# Revit family: Electronics_Commercial-Loudspeakers_Biamp_Small-Design-Loudspeaker_OVO5T
name_source: partatom
category: Communication Devices
units: mm (PartAtom-declared; Revit-internal decimal feet)

## family parameters
Cut with Voids When Loaded = No
Host = Face
Maintain Annotation Orientation = No
OmniClass Number = 23.85.10.11.14.14.14
Part Type = Normal
Room Calculation Point = No
Round Connector Dimension = Use Diameter
Shared = No

## types (2) — shared parameters
Compliance = IEC 62368-1 certified
Connector Description = Spring terminals; 25 V 40 W 16 Ω Nominal Impedance, 70/100V operation
Controls = Wattage / low impedance selector switch
Depth = 7.09 "
Environmental Rating = IP40 per IEC 60529
Height = 10.24 "
Input Connections = Spring-lever terminals with wiring cover
Manufacturer = Biamp
Mounting Provisions = Pan and tilt U-bracket
Nominal Beamwidth  (H x V) = 130° x 100°
Nominal Continuous Power Handling = 25 V  (40 W, 16 Ω Nominal Impedance)
Nominal Maximum SPL (Processed) = Peak: 108 dB - Continuous: 102 dB
Operating Environment = Indoor
Operating Mode = Passive with selectable low-impedance or 70 V/100 V operation, single amplified with DSP
Operating Range (-10 dB) = 74 Hz to 20 kHz
Product Documentation Link = https://downloads.biamp.com
Product Page URL = https://www.biamp.com
Product data url = https://bimobject.com
Rated Continuous Voltage = 20.0 V (26 dBV)
Rated Maximum SPL (Processed) = Peak: 112 dB - Continuous: 100 dB
Recommended Amplifiers = 40 W - 80 W, 8 Ω (18 V - 25 V)
Required Accessories = 80 Hz, 12 dB / oct. Butterworth high pass filter; DSP preset
Sensitivity = 86 dB (2.83 V); 89 dB (1 W, 16 Ω)
Shipping Weight = 17.75 lbf
Transducers = LF 1 x 5.25 (133 mm) coated paper cone, HF 1 x 1 (25 mm) silk dome tweeter
Transformer = 70 V: 30 W, 15 W, 7.5 W, 3 W, 1.5 W; 100 V: 30 W, 15 W, 7.5 W, 3 W
URL = https://www.biamp.com
Weight = 6.80 lbf
Width = 6.69 "
zero-valued in all types: Default Elevation

## per-type parameters (varying)
| type | Description | Grill Material | Housing Material | Mounting Material |
| OVO5T B | OVO5T-B 5.25" Design Two-Way Loudspeaker, Black | Biamp - Plastic - Black(Grid) | Biamp - Plastic - Black | Biamp - Metal - Black |
| OVO5T W | OVO5T-W 5.25" Design Two-Way Loudspeaker, Black | Biamp - Plastic - White(Grid) | Biamp - Plastic - White | Biamp - Metal - White |

note: column(s) folded — value = type name in every type: Model

## geometry (parser evidence)
native form markers: Blend x2, Sweep x14
no freeform markers — native parametric forms only
